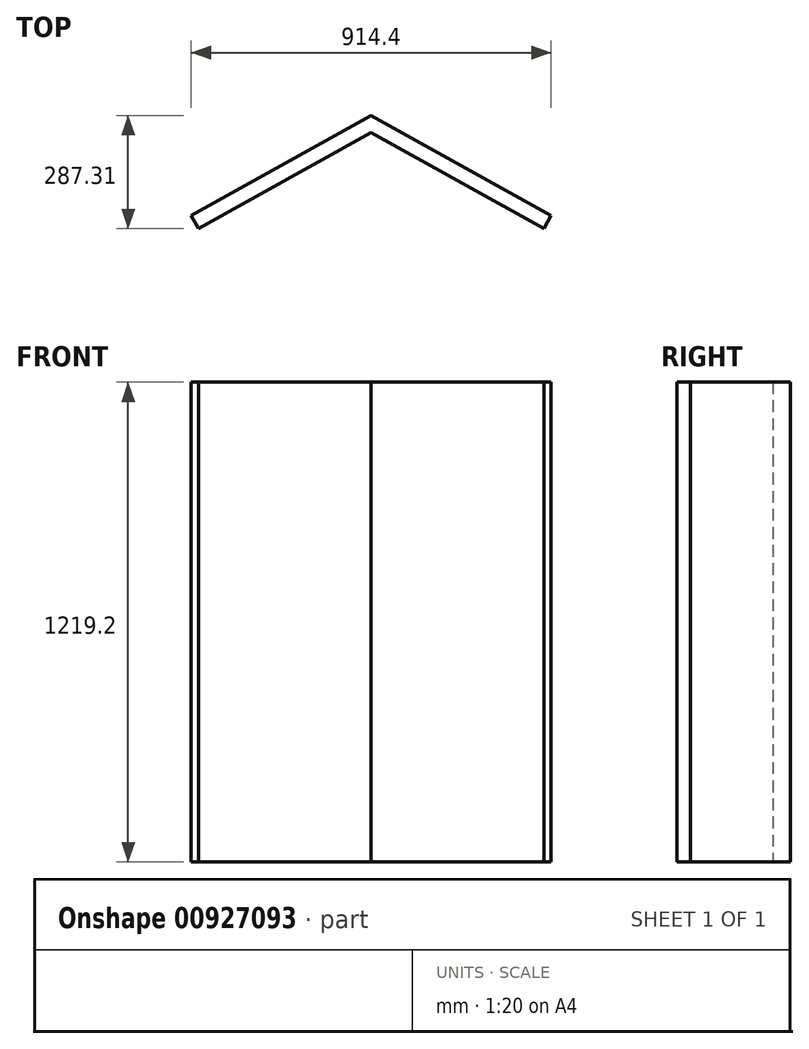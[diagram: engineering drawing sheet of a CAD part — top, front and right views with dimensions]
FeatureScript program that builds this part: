
annotation { "Feature Type Name" : "Feature", "Feature Type Description" : "" }
export const myFeature = defineFeature(function(context is Context, id is Id, definition is map)
    precondition{}
    {
        {
            var Q0;
            Q0=qCreatedBy(makeId("Top.planeOp"),FACE);
            var sketch = newSketch(context, id + "F0", { "sketchPlane" : qUnion([Q0])});
            skLineSegment(sketch, "E0", {"start": v(457.2, 0) * mm, "end": v(0, 254) * mm});
            skLineSegment(sketch, "E1", {"start": v(0, 254) * mm, "end": v(-457.2, 0) * mm});
            skLineSegment(sketch, "E2", {"start": v(0, 210.42) * mm, "end": v(438.7, -33.3) * mm});
            skLineSegment(sketch, "E3", {"start": v(438.7, -33.3) * mm, "end": v(457.2, 0) * mm});
            skLineSegment(sketch, "E4", {"start": v(0, 210.42) * mm, "end": v(-438.7, -33.3) * mm});
            skLineSegment(sketch, "E5", {"start": v(-438.7, -33.3) * mm, "end": v(-457.2, 0) * mm});
            skSolve(sketch);
        }
        {
            var Q0;
            Q0 = qSketchRegion(id + "F0", true);
            extrude(context, id + "F1", {"entities" : qUnion([Q0]), "depth" : 1219.2 * mm, "offsetDistance" : 25.4 * mm});
        }
    });
